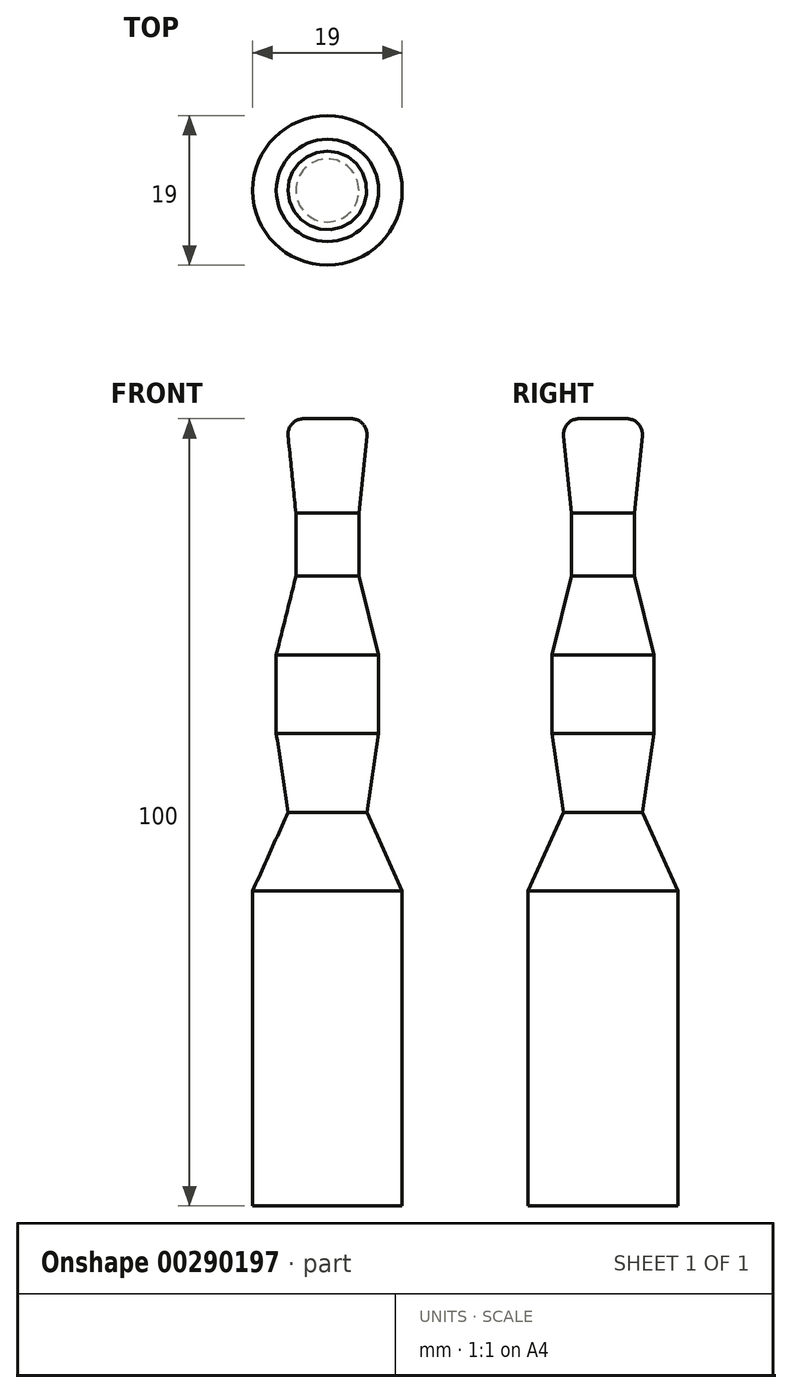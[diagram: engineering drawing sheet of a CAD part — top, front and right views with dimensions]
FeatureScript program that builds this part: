
annotation { "Feature Type Name" : "Feature", "Feature Type Description" : "" }
export const myFeature = defineFeature(function(context is Context, id is Id, definition is map)
    precondition{}
    {
        {
            var Q0;
            Q0=qCreatedBy(makeId("Front.planeOp"),FACE);
            var sketch = newSketch(context, id + "F0", { "sketchPlane" : qUnion([Q0])});
            skLineSegment(sketch, "E0", {"start": v(0, 0) * mm, "end": v(3.01, 0) * mm});
            skArc(sketch, "E1", {"start": v(5, -2.2) * mm, "mid": v(4.5, -0.66) * mm, "end": v(3.01, 0) * mm});
            skLineSegment(sketch, "E2", {"start": v(5, -2.2) * mm, "end": v(4, -12) * mm});
            skLineSegment(sketch, "E3", {"start": v(4, -12) * mm, "end": v(4, -20) * mm});
            skLineSegment(sketch, "E4", {"start": v(4, -20) * mm, "end": v(6.5, -30) * mm});
            skLineSegment(sketch, "E5", {"start": v(6.5, -30) * mm, "end": v(6.5, -40) * mm});
            skLineSegment(sketch, "E6", {"start": v(6.5, -40) * mm, "end": v(5, -50) * mm});
            skLineSegment(sketch, "E7", {"start": v(5, -50) * mm, "end": v(9.5, -60) * mm});
            skLineSegment(sketch, "E8", {"start": v(9.5, -60) * mm, "end": v(9.5, -100) * mm});
            skLineSegment(sketch, "E9", {"start": v(9.5, -100) * mm, "end": v(0, -100) * mm});
            skLineSegment(sketch, "E10", {"start": v(0, -100) * mm, "end": v(0, 0) * mm});
            skSolve(sketch);
        }
        {
            var Q0;
            Q0 = qSketchRegion(id + "F0", true);
            var Q1;
            Q1=sQuery(id+"F0.wireOp",EDGE,"E10");
            revolve(context, id + "F1", {"entities" : qUnion([Q0]), "axis" : qUnion([Q1]), "revolveType" : RevolveType.FULL});
        }
    });
